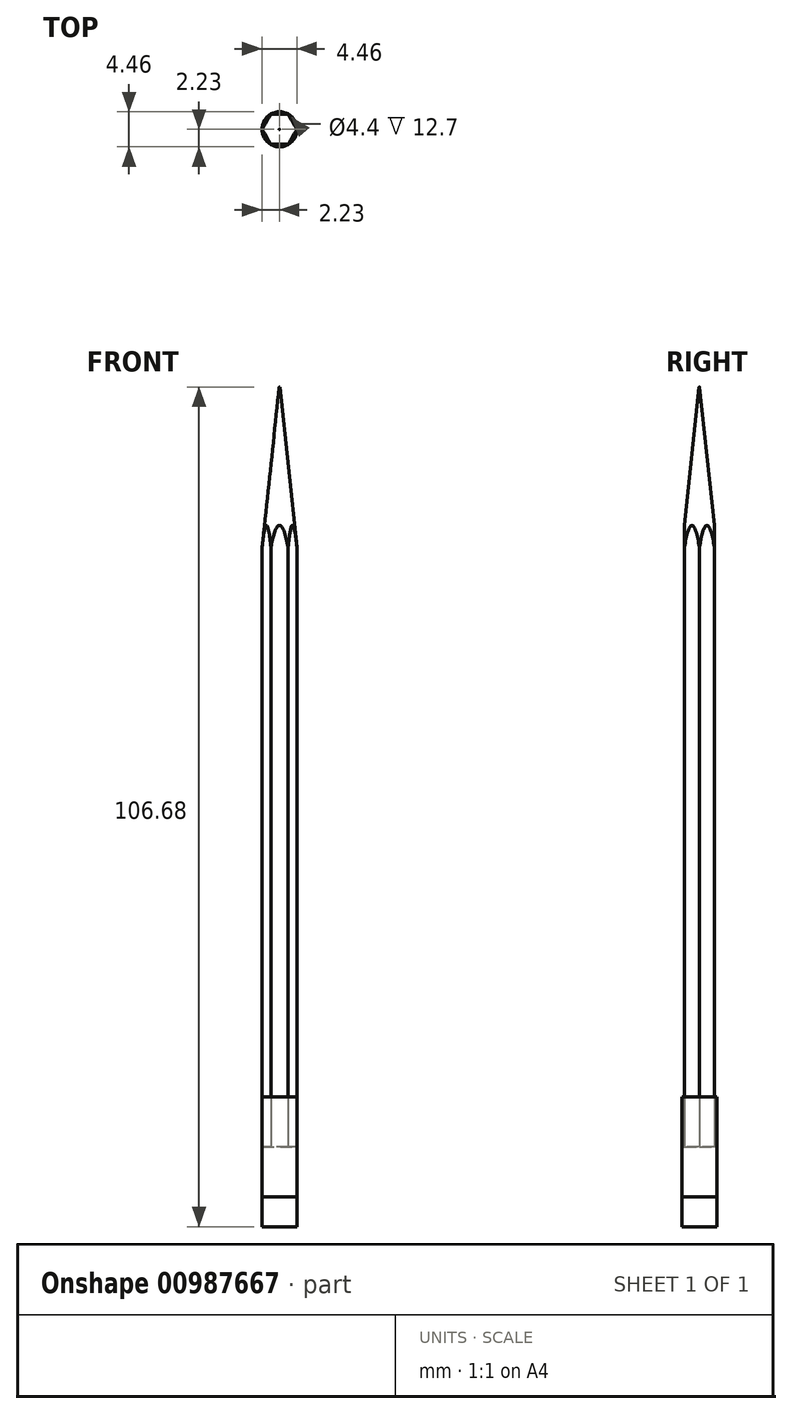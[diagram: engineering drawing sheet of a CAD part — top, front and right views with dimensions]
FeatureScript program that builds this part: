
annotation { "Feature Type Name" : "Feature", "Feature Type Description" : "" }
export const myFeature = defineFeature(function(context is Context, id is Id, definition is map)
    precondition{}
    {
        {
            var Q0;
            Q0=qCreatedBy(makeId("Top.planeOp"),FACE);
            var sketch = newSketch(context, id + "F0", { "sketchPlane" : qUnion([Q0])});
            skCircle(sketch, "E0", {"center": v(0, 0) * mm, "radius": 1.9 * mm});
            skCircle(sketch, "E1.cCircle", {"center": v(0, 0) * mm, "radius": 1.9 * mm, "construction": true});
            skLineSegment(sketch, "E1.0", {"start": v(1.1, -1.9) * mm, "end": v(-1.1, -1.9) * mm});
            skLineSegment(sketch, "E1.1", {"start": v(-1.1, -1.9) * mm, "end": v(-2.2, 0) * mm});
            skLineSegment(sketch, "E1.2", {"start": v(-2.2, 0) * mm, "end": v(-1.1, 1.9) * mm});
            skLineSegment(sketch, "E1.3", {"start": v(-1.1, 1.9) * mm, "end": v(1.1, 1.9) * mm});
            skLineSegment(sketch, "E1.4", {"start": v(1.1, 1.9) * mm, "end": v(2.2, 0) * mm});
            skLineSegment(sketch, "E1.5", {"start": v(2.2, 0) * mm, "end": v(1.1, -1.9) * mm});
            skPoint(sketch, "E1.0.midPoint", {"position": v(0, -1.9) * mm});
            skSolve(sketch);
        }
        {
            var Q0;
            {var subQ0=sQuery(id+"F0.wireOp",EDGE,"E0");var subQ4=makeQuery(id+"F0.imprint","INTERSECT",VERTEX,{"derivedFrom":[subQ0,sQuery(id+"F0.wireOp",EDGE,"E1.3")]});Q0=makeQuery(id+"F0.imprint","IMPRINT",FACE,{"disambiguationData":[TD([[makeQuery(id+"F0.imprint","IMPRINT",EDGE,{"disambiguationData":[TD([[subQ4,1.0]])],"derivedFrom":subQ0}),1.0]])]});}
            var Q1;
            {var subQ0=sQuery(id+"F0.wireOp",EDGE,"E1.3");var subQ1=sQuery(id+"F0.wireOp",EDGE,"E0");var subQ2=makeQuery(id+"F0.imprint","INTERSECT",VERTEX,{"derivedFrom":[subQ1,subQ0]});Q1=makeQuery(id+"F0.imprint","IMPRINT",FACE,{"disambiguationData":[TD([[makeQuery(id+"F0.imprint","IMPRINT",EDGE,{"disambiguationData":[TD([[subQ2,-1.0]])],"derivedFrom":subQ1}),-1.0]])]});}
            var Q2;
            {var subQ0=sQuery(id+"F0.wireOp",EDGE,"E1.2");var subQ1=sQuery(id+"F0.wireOp",EDGE,"E0");var subQ2=makeQuery(id+"F0.imprint","INTERSECT",VERTEX,{"derivedFrom":[subQ1,subQ0]});Q2=makeQuery(id+"F0.imprint","IMPRINT",FACE,{"disambiguationData":[TD([[makeQuery(id+"F0.imprint","IMPRINT",EDGE,{"disambiguationData":[TD([[subQ2,-1.0]])],"derivedFrom":subQ1}),-1.0]])]});}
            var Q3;
            {var subQ0=sQuery(id+"F0.wireOp",EDGE,"E1.1");var subQ1=sQuery(id+"F0.wireOp",EDGE,"E0");var subQ2=makeQuery(id+"F0.imprint","INTERSECT",VERTEX,{"derivedFrom":[subQ1,subQ0]});Q3=makeQuery(id+"F0.imprint","IMPRINT",FACE,{"disambiguationData":[TD([[makeQuery(id+"F0.imprint","IMPRINT",EDGE,{"disambiguationData":[TD([[subQ2,-1.0]])],"derivedFrom":subQ1}),-1.0]])]});}
            var Q4;
            {var subQ0=sQuery(id+"F0.wireOp",EDGE,"E1.0");var subQ1=sQuery(id+"F0.wireOp",EDGE,"E0");var subQ2=makeQuery(id+"F0.imprint","INTERSECT",VERTEX,{"derivedFrom":[subQ1,subQ0]});Q4=makeQuery(id+"F0.imprint","IMPRINT",FACE,{"disambiguationData":[TD([[makeQuery(id+"F0.imprint","IMPRINT",EDGE,{"disambiguationData":[TD([[subQ2,-1.0]])],"derivedFrom":subQ1}),-1.0]])]});}
            var Q5;
            {var subQ0=sQuery(id+"F0.wireOp",EDGE,"E1.4");var subQ1=sQuery(id+"F0.wireOp",EDGE,"E0");var subQ2=makeQuery(id+"F0.imprint","INTERSECT",VERTEX,{"derivedFrom":[subQ1,subQ0]});Q5=makeQuery(id+"F0.imprint","IMPRINT",FACE,{"disambiguationData":[TD([[makeQuery(id+"F0.imprint","IMPRINT",EDGE,{"disambiguationData":[TD([[subQ2,1.0]])],"derivedFrom":subQ1}),-1.0]])]});}
            var Q6;
            {var subQ0=sQuery(id+"F0.wireOp",EDGE,"E1.3");var subQ1=sQuery(id+"F0.wireOp",EDGE,"E0");var subQ2=makeQuery(id+"F0.imprint","INTERSECT",VERTEX,{"derivedFrom":[subQ1,subQ0]});Q6=makeQuery(id+"F0.imprint","IMPRINT",FACE,{"disambiguationData":[TD([[makeQuery(id+"F0.imprint","IMPRINT",EDGE,{"disambiguationData":[TD([[subQ2,1.0]])],"derivedFrom":subQ1}),-1.0]])]});}
            extrude(context, id + "F1", {"entities" : qUnion([Q0, Q1, Q2, Q3, Q4, Q5, Q6]), "depth" : 76.2 * mm, "offsetDistance" : 25.4 * mm});
        }
        {
            var Q0;
            Q0=makeQuery(id+"F1.opExtrude","CAP_FACE",FACE,{"disambiguationData":[OSD([sQuery(id+"F0.wireOp",EDGE,"E1.0"),sQuery(id+"F0.wireOp",EDGE,"E1.1"),sQuery(id+"F0.wireOp",EDGE,"E1.2"),sQuery(id+"F0.wireOp",EDGE,"E1.3"),sQuery(id+"F0.wireOp",EDGE,"E1.4"),sQuery(id+"F0.wireOp",EDGE,"E1.5")])],"isStart":false});
            extrude(context, id + "F2", {"entities" : qUnion([Q0]), "operationType" : NewBodyOperationType.ADD, "depth" : 20.32 * mm, "offsetDistance" : 25.4 * mm});
        }
        {
            var Q0;
            Q0=qCreatedBy(makeId("Front.planeOp"),FACE);
            var sketch = newSketch(context, id + "F3", { "sketchPlane" : qUnion([Q0])});
            skLineSegment(sketch, "E2", {"start": v(-2.2, 76.2) * mm, "end": v(-2.2, 96.52) * mm});
            skLineSegment(sketch, "E3", {"start": v(-0.04, 96.52) * mm, "end": v(-2.2, 96.52) * mm});
            skLineSegment(sketch, "E4", {"start": v(-0.04, 96.52) * mm, "end": v(-2.2, 76.2) * mm});
            skSolve(sketch);
        }
        {
            var Q0;
            Q0=qCreatedBy(makeId("Right.planeOp"),FACE);
            var sketch = newSketch(context, id + "F4", { "sketchPlane" : qUnion([Q0])});
            skLineSegment(sketch, "E5", {"start": v(0, 96.63) * mm, "end": v(0, 0) * mm, "construction": true});
            skSolve(sketch);
        }
        {
            var Q0;
            Q0 = qSketchRegion(id + "F3", true);
            var Q1;
            Q1=sQuery(id+"F4.wireOp",EDGE,"E5");
            revolve(context, id + "F5", {"operationType" : NewBodyOperationType.REMOVE, "surfaceOperationType" : NewSurfaceOperationType.NEW, "entities" : qUnion([Q0]), "axis" : qUnion([Q1]), "revolveType" : RevolveType.FULL, "oppositeDirection" : true});
        }
        {
            var Q0;
            Q0=makeQuery(id+"F1.opExtrude","CAP_FACE",FACE,{"disambiguationData":[OSD([sQuery(id+"F0.wireOp",EDGE,"E1.0"),sQuery(id+"F0.wireOp",EDGE,"E1.1"),sQuery(id+"F0.wireOp",EDGE,"E1.2"),sQuery(id+"F0.wireOp",EDGE,"E1.3"),sQuery(id+"F0.wireOp",EDGE,"E1.4"),sQuery(id+"F0.wireOp",EDGE,"E1.5")])],"isStart":true});
            var sketch = newSketch(context, id + "F6", { "sketchPlane" : qUnion([Q0])});
            skCircle(sketch, "E6", {"center": v(0, 0) * mm, "radius": 2.2 * mm});
            skCircle(sketch, "E7", {"center": v(0, 0) * mm, "radius": 2.23 * mm});
            skSolve(sketch);
        }
        {
            var Q0;
            Q0=makeQuery(id+"F6.imprint","IMPRINT",FACE,{"disambiguationData":[TD([[makeQuery(id+"F6.imprint","IMPRINT",EDGE,{"derivedFrom":sQuery(id+"F6.wireOp",EDGE,"E7")}),1.0]])]});
            extrude(context, id + "F7", {"entities" : qUnion([Q0]), "endBound" : BoundingType.SYMMETRIC, "depth" : 12.7 * mm, "offsetDistance" : 25.4 * mm});
        }
        {
            var Q0;
            {var subQ1=makeQuery(id+"F1.opExtrude","CAP_EDGE",EDGE,{"disambiguationData":[OSD([sQuery(id+"F0.wireOp",EDGE,"E1.4")])],"isStart":true});Q0=makeQuery(id+"F6.imprint","IMPRINT",FACE,{"disambiguationData":[TD([[makeQuery(id+"F6.imprint","IMPRINT",EDGE,{"derivedFrom":subQ1}),-1.0]])]});}
            var Q1;
            {var subQ1=makeQuery(id+"F1.opExtrude","CAP_EDGE",EDGE,{"disambiguationData":[OSD([sQuery(id+"F0.wireOp",EDGE,"E1.3")])],"isStart":true});Q1=makeQuery(id+"F6.imprint","IMPRINT",FACE,{"disambiguationData":[TD([[makeQuery(id+"F6.imprint","IMPRINT",EDGE,{"derivedFrom":subQ1}),-1.0]])]});}
            var Q2;
            Q2=makeQuery(id+"F6.imprint","IMPRINT",FACE,{"disambiguationData":[TD([[makeQuery(id+"F6.imprint","IMPRINT",EDGE,{"derivedFrom":makeQuery(id+"F1.opExtrude","CAP_EDGE",EDGE,{"disambiguationData":[OSD([sQuery(id+"F0.wireOp",EDGE,"E1.0")])],"isStart":true})}),1.0]])]});
            var Q3;
            {var subQ1=makeQuery(id+"F1.opExtrude","CAP_EDGE",EDGE,{"disambiguationData":[OSD([sQuery(id+"F0.wireOp",EDGE,"E1.2")])],"isStart":true});Q3=makeQuery(id+"F6.imprint","IMPRINT",FACE,{"disambiguationData":[TD([[makeQuery(id+"F6.imprint","IMPRINT",EDGE,{"derivedFrom":subQ1}),-1.0]])]});}
            var Q4;
            {var subQ1=makeQuery(id+"F1.opExtrude","CAP_EDGE",EDGE,{"disambiguationData":[OSD([sQuery(id+"F0.wireOp",EDGE,"E1.1")])],"isStart":true});Q4=makeQuery(id+"F6.imprint","IMPRINT",FACE,{"disambiguationData":[TD([[makeQuery(id+"F6.imprint","IMPRINT",EDGE,{"derivedFrom":subQ1}),-1.0]])]});}
            var Q5;
            {var subQ1=makeQuery(id+"F1.opExtrude","CAP_EDGE",EDGE,{"disambiguationData":[OSD([sQuery(id+"F0.wireOp",EDGE,"E1.5")])],"isStart":true});Q5=makeQuery(id+"F6.imprint","IMPRINT",FACE,{"disambiguationData":[TD([[makeQuery(id+"F6.imprint","IMPRINT",EDGE,{"derivedFrom":subQ1}),-1.0]])]});}
            var Q6;
            {var subQ1=makeQuery(id+"F1.opExtrude","CAP_EDGE",EDGE,{"disambiguationData":[OSD([sQuery(id+"F0.wireOp",EDGE,"E1.0")])],"isStart":true});Q6=makeQuery(id+"F6.imprint","IMPRINT",FACE,{"disambiguationData":[TD([[makeQuery(id+"F6.imprint","IMPRINT",EDGE,{"derivedFrom":subQ1}),-1.0]])]});}
            extrude(context, id + "F8", {"entities" : qUnion([Q0, Q1, Q2, Q3, Q4, Q5, Q6]), "depth" : 10.16 * mm, "offsetDistance" : 25.4 * mm});
        }
    });
